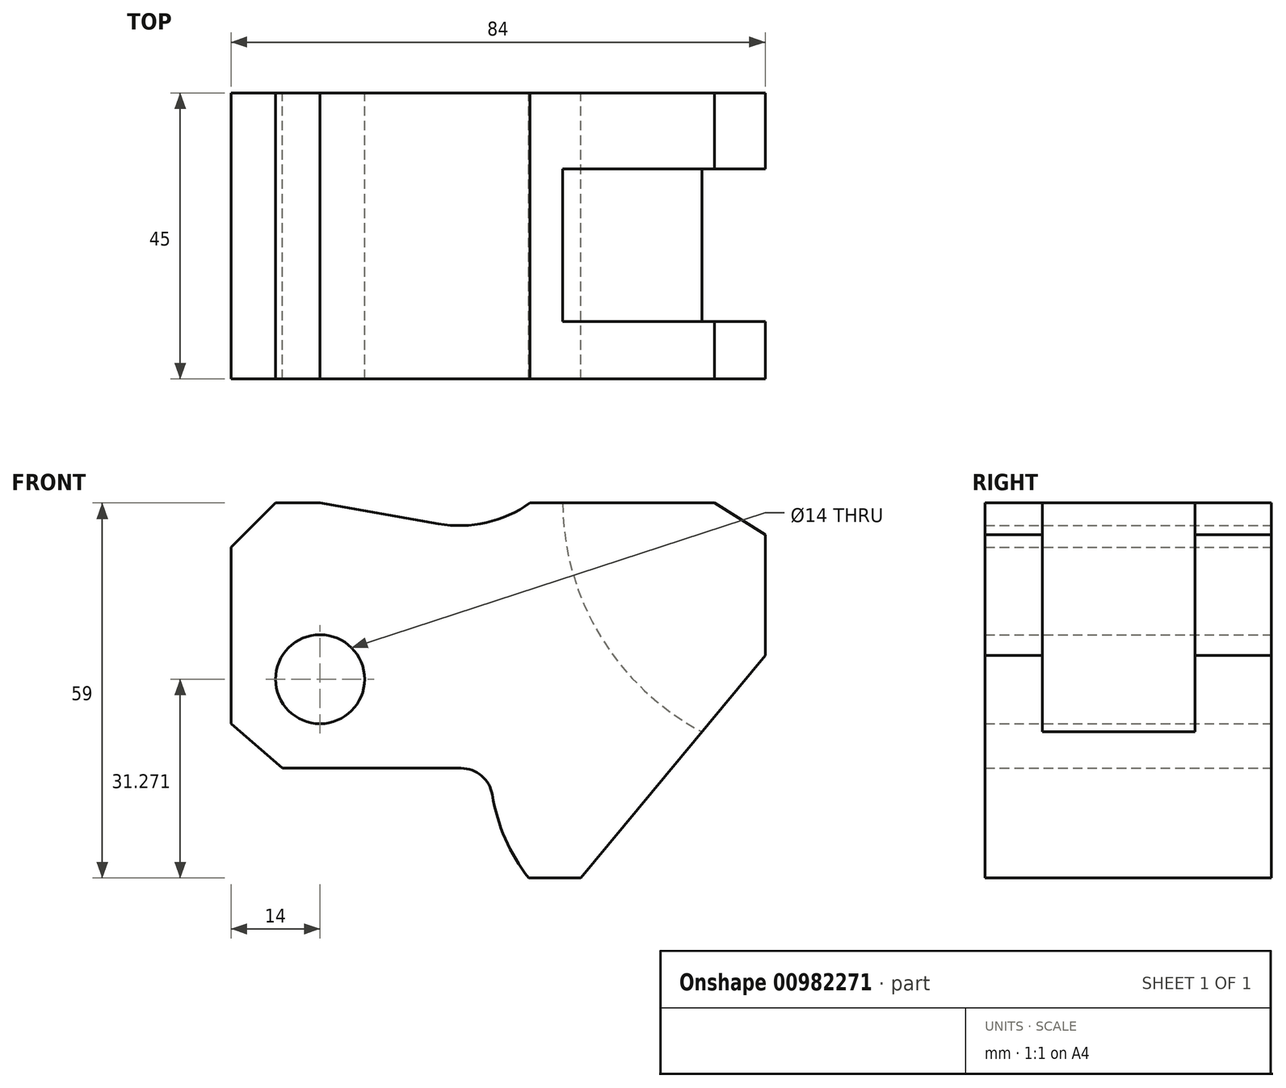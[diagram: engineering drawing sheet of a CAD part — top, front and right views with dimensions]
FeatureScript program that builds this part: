
annotation { "Feature Type Name" : "Feature", "Feature Type Description" : "" }
export const myFeature = defineFeature(function(context is Context, id is Id, definition is map)
    precondition{}
    {
        {
            var Q0;
            Q0=qCreatedBy(makeId("Front.planeOp"),FACE);
            var sketch = newSketch(context, id + "F0", { "sketchPlane" : qUnion([Q0])});
            skLineSegment(sketch, "E0.left", {"start": v(-40.5, 21.5) * mm, "end": v(-40.5, -6.23) * mm});
            skPoint(sketch, "E0.middle", {"position": v(0, 0) * mm});
            skLineSegment(sketch, "E1", {"start": v(35.5, 28.5) * mm, "end": v(43.5, 23.5) * mm});
            skLineSegment(sketch, "E2", {"start": v(43.5, 4.5) * mm, "end": v(14.5, -30.5) * mm});
            skArc(sketch, "E3", {"start": v(0.6, -17.42) * mm, "mid": v(2.62, -24.32) * mm, "end": v(6.29, -30.5) * mm});
            skLineSegment(sketch, "E4", {"start": v(-32.4, -13.23) * mm, "end": v(-40.5, -6.23) * mm});
            skLineSegment(sketch, "E5", {"start": v(-32.4, -13.23) * mm, "end": v(-4.34, -13.23) * mm});
            skCircle(sketch, "E6", {"center": v(-26.5, 0.77) * mm, "radius": 7 * mm});
            skLineSegment(sketch, "E7", {"start": v(-40.5, 21.5) * mm, "end": v(-33.5, 28.5) * mm});
            skLineSegment(sketch, "E8", {"start": v(-33.5, 28.5) * mm, "end": v(-26.5, 28.5) * mm});
            skLineSegment(sketch, "E9", {"start": v(-26.5, 28.5) * mm, "end": v(-7.89, 25.22) * mm});
            skArc(sketch, "E10.filletArc", {"start": v(0.6, -17.42) * mm, "mid": v(-1.1, -14.42) * mm, "end": v(-4.34, -13.23) * mm});
            skLineSegment(sketch, "E11", {"start": v(35.5, 28.5) * mm, "end": v(6.5, 28.5) * mm});
            skArc(sketch, "E12", {"start": v(-7.89, 25.22) * mm, "mid": v(-0.36, 25.4) * mm, "end": v(6.5, 28.5) * mm});
            skLineSegment(sketch, "E13", {"start": v(43.5, 4.5) * mm, "end": v(43.5, 23.5) * mm});
            skLineSegment(sketch, "E14", {"start": v(6.29, -30.5) * mm, "end": v(14.5, -30.5) * mm});
            skSolve(sketch);
        }
        {
            var Q0;
            Q0 = qSketchRegion(id + "F0", true);
            extrude(context, id + "F1", {"entities" : qUnion([Q0]), "depth" : 45 * mm, "offsetDistance" : 25 * mm});
        }
        {
            var Q0;
            Q0=makeQuery(id+"F1.opExtrude","CAP_FACE",FACE,{"disambiguationData":[OSD([sQuery(id+"F0.wireOp",EDGE,"E0.left"),sQuery(id+"F0.wireOp",EDGE,"E1"),sQuery(id+"F0.wireOp",EDGE,"E2"),sQuery(id+"F0.wireOp",EDGE,"E3"),sQuery(id+"F0.wireOp",EDGE,"E4"),sQuery(id+"F0.wireOp",EDGE,"E5"),sQuery(id+"F0.wireOp",EDGE,"E6"),sQuery(id+"F0.wireOp",EDGE,"E7"),sQuery(id+"F0.wireOp",EDGE,"E8"),sQuery(id+"F0.wireOp",EDGE,"E9"),sQuery(id+"F0.wireOp",EDGE,"E10.filletArc"),sQuery(id+"F0.wireOp",EDGE,"E11"),sQuery(id+"F0.wireOp",EDGE,"E12"),sQuery(id+"F0.wireOp",EDGE,"E13"),sQuery(id+"F0.wireOp",EDGE,"E14")])],"isStart":false});
            cPlane(context, id + "F2", {"entities" : qUnion([Q0]), "cplaneType" : CPlaneType.OFFSET, "offset" : 22.5 * mm, "oppositeDirection" : true, "width" : 150 * mm, "height" : 150 * mm});
        }
        {
            var Q0;
            Q0=qCreatedBy(id+"F2.planeOp",FACE);
            var sketch = newSketch(context, id + "F3", { "sketchPlane" : qUnion([Q0])});
            skPoint(sketch, "E15.middle", {"position": v(0, 0) * mm});
            skArc(sketch, "E16", {"start": v(11.64, 28.5) * mm, "mid": v(17.62, 7.47) * mm, "end": v(33.56, -7.5) * mm});
            skLineSegment(sketch, "E17", {"start": v(11.64, 28.5) * mm, "end": v(35.5, 28.5) * mm});
            skLineSegment(sketch, "E18", {"start": v(35.5, 28.5) * mm, "end": v(43.5, 23.5) * mm});
            skLineSegment(sketch, "E19", {"start": v(43.5, 23.5) * mm, "end": v(43.5, 4.5) * mm});
            skLineSegment(sketch, "E20", {"start": v(43.5, 4.5) * mm, "end": v(33.56, -7.5) * mm});
            skSolve(sketch);
        }
        {
            var Q0;
            Q0 = qSketchRegion(id + "F3", true);
            extrude(context, id + "F4", {"entities" : qUnion([Q0]), "operationType" : NewBodyOperationType.REMOVE, "oppositeDirection" : true, "depth" : 10.5 * mm, "offsetDistance" : 25 * mm, "hasSecondDirection" : true, "secondDirectionOppositeDirection" : false, "secondDirectionDepth" : 13.5 * mm});
        }
    });
